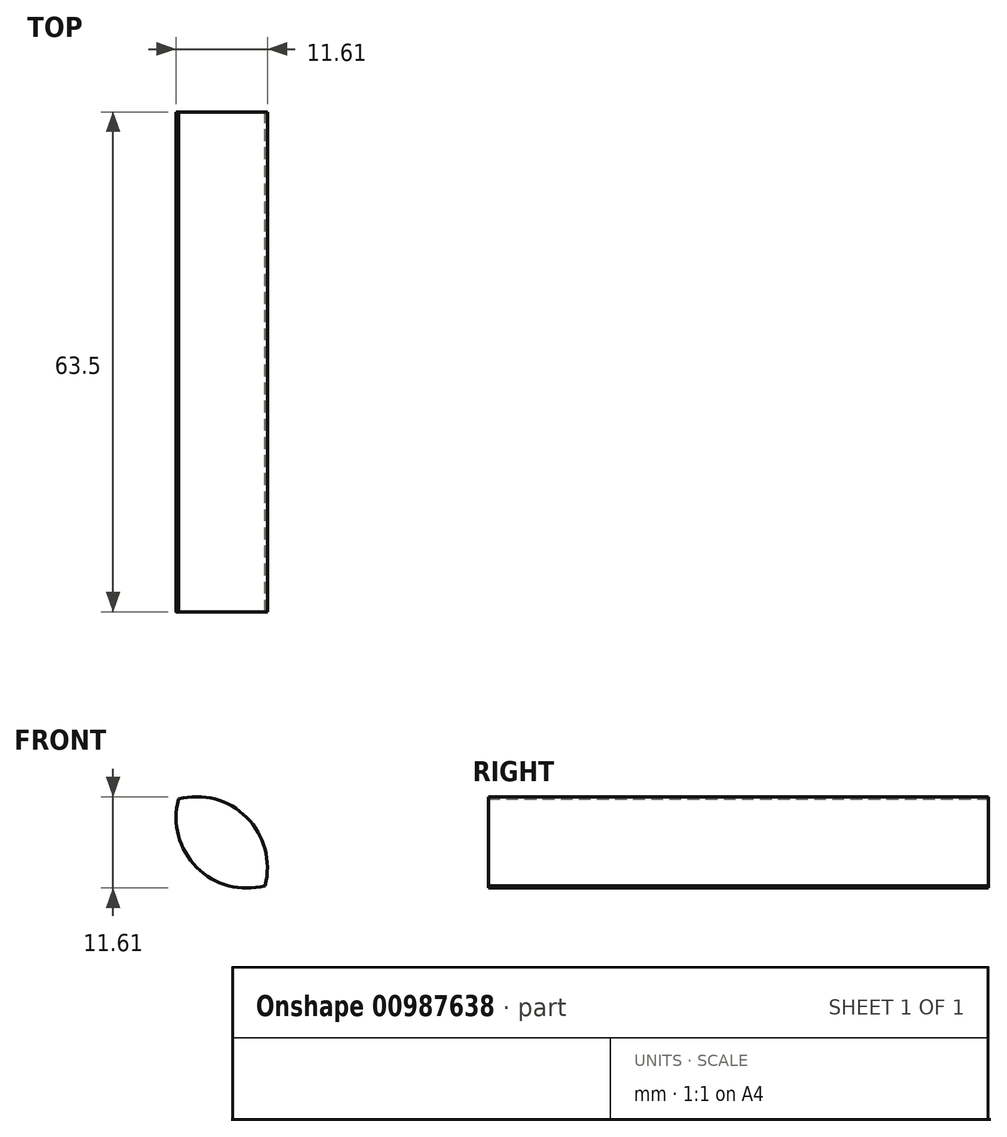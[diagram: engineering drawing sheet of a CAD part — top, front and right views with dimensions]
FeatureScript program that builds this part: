
annotation { "Feature Type Name" : "Feature", "Feature Type Description" : "" }
export const myFeature = defineFeature(function(context is Context, id is Id, definition is map)
    precondition{}
    {
        {
            var Q0;
            Q0=qCreatedBy(makeId("Front.planeOp"),FACE);
            var sketch = newSketch(context, id + "F0", { "sketchPlane" : qUnion([Q0])});
            skCircle(sketch, "E0", {"center": v(0, 0) * mm, "radius": 8.98 * mm});
            skCircle(sketch, "E1", {"center": v(6.35, 6.35) * mm, "radius": 8.98 * mm});
            skSolve(sketch);
        }
        {
            var Q0;
            {var subQ0=sQuery(id+"F0.wireOp",EDGE,"E1");var subQ1=sQuery(id+"F0.wireOp",EDGE,"E0");var subQ2=makeQuery(id+"F0.imprint","INTERSECT",VERTEX,{"disambiguationData":[OD(0.0)],"derivedFrom":[subQ1,subQ0]});Q0=makeQuery(id+"F0.imprint","IMPRINT",FACE,{"disambiguationData":[TD([[makeQuery(id+"F0.imprint","IMPRINT",EDGE,{"disambiguationData":[TD([[subQ2,1.0]])],"derivedFrom":subQ1}),1.0]])]});}
            extrude(context, id + "F1", {"entities" : qUnion([Q0]), "depth" : 63.5 * mm, "offsetDistance" : 25.4 * mm});
        }
    });
